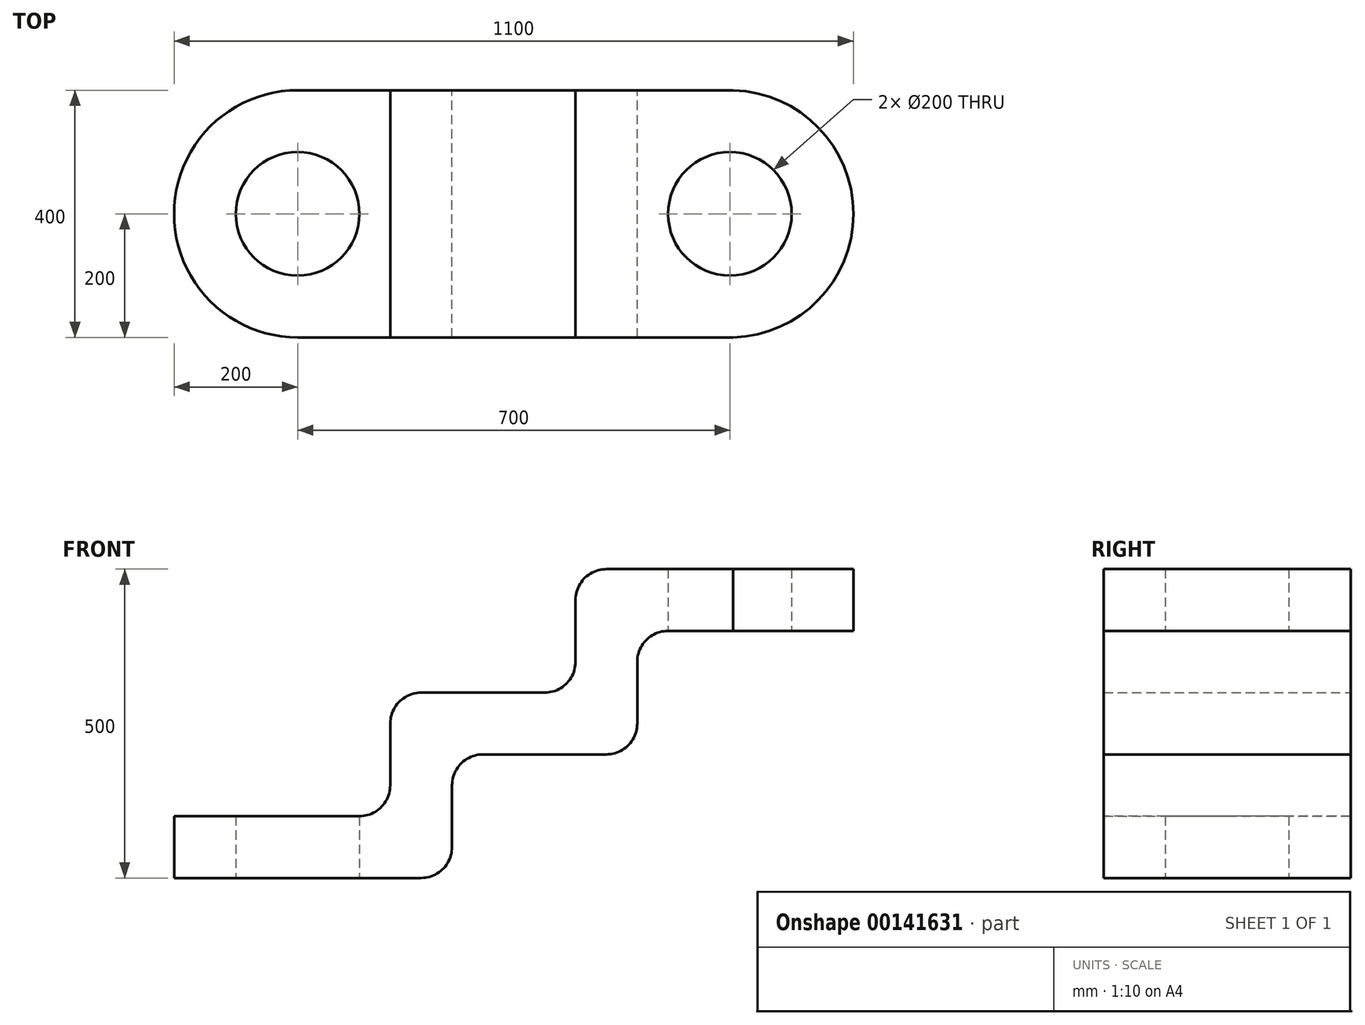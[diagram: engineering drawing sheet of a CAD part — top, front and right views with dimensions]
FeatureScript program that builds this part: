
annotation { "Feature Type Name" : "Feature", "Feature Type Description" : "" }
export const myFeature = defineFeature(function(context is Context, id is Id, definition is map)
    precondition{}
    {
        {
            var Q0;
            Q0=qCreatedBy(makeId("Top.planeOp"),FACE);
            var sketch = newSketch(context, id + "F0", { "sketchPlane" : qUnion([Q0])});
            skCircle(sketch, "E0", {"center": v(-350, 0) * mm, "radius": 100 * mm});
            skLineSegment(sketch, "E1", {"start": v(0, 0) * mm, "end": v(0, 164.51) * mm, "construction": true});
            skCircle(sketch, "E2.MirrorC", {"center": v(350, 0) * mm, "radius": 100 * mm});
            skArc(sketch, "E3", {"start": v(-349.98, 200) * mm, "mid": v(-550, 0) * mm, "end": v(-349.98, -200) * mm});
            skArc(sketch, "E4.MirrorC", {"start": v(344.9, 199.93) * mm, "mid": v(550, 0) * mm, "end": v(344.9, -199.93) * mm});
            skLineSegment(sketch, "E5", {"start": v(355.14, 199.93) * mm, "end": v(-349.98, 200) * mm});
            skLineSegment(sketch, "E6.MirrorCS", {"start": v(355.14, -199.93) * mm, "end": v(-349.98, -200) * mm});
            skSolve(sketch);
        }
        {
            var Q0;
            Q0=makeQuery(id+"F0.imprint","IMPRINT",FACE,{"disambiguationData":[TD([[makeQuery(id+"F0.imprint","IMPRINT",EDGE,{"derivedFrom":sQuery(id+"F0.wireOp",EDGE,"E0")}),-1.0]])]});
            extrude(context, id + "F1", {"entities" : qUnion([Q0]), "depth" : 500 * mm});
        }
        {
            var Q0;
            Q0=qCreatedBy(makeId("Front.planeOp"),FACE);
            var sketch = newSketch(context, id + "F2", { "sketchPlane" : qUnion([Q0])});
            skLineSegment(sketch, "E7", {"start": v(-550, 0) * mm, "end": v(-150, 0) * mm});
            skLineSegment(sketch, "E8.0", {"start": v(-550, 100) * mm, "end": v(-250, 100) * mm});
            skLineSegment(sketch, "E9.0", {"start": v(-150, 300) * mm, "end": v(50, 300) * mm});
            skLineSegment(sketch, "E10.0", {"start": v(150, 500) * mm, "end": v(550, 500) * mm});
            skLineSegment(sketch, "E11", {"start": v(-550, 0) * mm, "end": v(-550, 100) * mm});
            skLineSegment(sketch, "E12.0", {"start": v(-100, 50) * mm, "end": v(-100, 150) * mm});
            skLineSegment(sketch, "E13.0", {"start": v(-200, 150) * mm, "end": v(-200, 250) * mm});
            skLineSegment(sketch, "E14.0", {"start": v(100, 350) * mm, "end": v(100, 450) * mm});
            skLineSegment(sketch, "E15.0", {"start": v(200, 250) * mm, "end": v(200, 350) * mm});
            skLineSegment(sketch, "E16.trimOffspring", {"start": v(-50, 200) * mm, "end": v(150, 200) * mm});
            skLineSegment(sketch, "E17", {"start": v(550, 500) * mm, "end": v(550, 400) * mm});
            skLineSegment(sketch, "E18.trimOffspring", {"start": v(250, 400) * mm, "end": v(550, 400) * mm});
            skPoint(sketch, "E19.visualSharp", {"position": v(-200, 100) * mm});
            skArc(sketch, "E19.filletArc", {"start": v(-250, 100) * mm, "mid": v(-214.64, 114.64) * mm, "end": v(-200, 150) * mm});
            skPoint(sketch, "E20.visualSharp", {"position": v(-200, 300) * mm});
            skArc(sketch, "E20.filletArc", {"start": v(-150, 300) * mm, "mid": v(-185.36, 285.36) * mm, "end": v(-200, 250) * mm});
            skPoint(sketch, "E21.visualSharp", {"position": v(-100, 0) * mm});
            skArc(sketch, "E21.filletArc", {"start": v(-150, 0) * mm, "mid": v(-114.64, 14.64) * mm, "end": v(-100, 50) * mm});
            skPoint(sketch, "E22.visualSharp", {"position": v(-100, 200) * mm});
            skArc(sketch, "E22.filletArc", {"start": v(-50, 200) * mm, "mid": v(-85.36, 185.36) * mm, "end": v(-100, 150) * mm});
            skPoint(sketch, "E23.visualSharp", {"position": v(100, 300) * mm});
            skArc(sketch, "E23.filletArc", {"start": v(50, 300) * mm, "mid": v(85.36, 314.64) * mm, "end": v(100, 350) * mm});
            skPoint(sketch, "E24.visualSharp", {"position": v(200, 200) * mm});
            skArc(sketch, "E24.filletArc", {"start": v(150, 200) * mm, "mid": v(185.36, 214.64) * mm, "end": v(200, 250) * mm});
            skPoint(sketch, "E25.visualSharp", {"position": v(100, 500) * mm});
            skArc(sketch, "E25.filletArc", {"start": v(150, 500) * mm, "mid": v(114.64, 485.36) * mm, "end": v(100, 450) * mm});
            skPoint(sketch, "E26.visualSharp", {"position": v(200, 400) * mm});
            skArc(sketch, "E26.filletArc", {"start": v(250, 400) * mm, "mid": v(214.64, 385.36) * mm, "end": v(200, 350) * mm});
            skSolve(sketch);
        }
        {
            var Q0;
            Q0=makeQuery(id+"F2.imprint","IMPRINT",FACE,{"disambiguationData":[TD([[makeQuery(id+"F2.imprint","IMPRINT",EDGE,{"derivedFrom":sQuery(id+"F2.wireOp",EDGE,"E7")}),1.0]])]});
            extrude(context, id + "F3", {"entities" : qUnion([Q0]), "endBound" : BoundingType.SYMMETRIC, "depth" : 600 * mm});
        }
        {
            var Q0;
            Q0=makeQuery(id+"F1.opExtrude","SWEPT_BODY",BODY,{"disambiguationData":[OSD([sQuery(id+"F0.wireOp",EDGE,"E0"),sQuery(id+"F0.wireOp",EDGE,"E2.MirrorC"),sQuery(id+"F0.wireOp",EDGE,"E3"),sQuery(id+"F0.wireOp",EDGE,"E4.MirrorC"),sQuery(id+"F0.wireOp",EDGE,"E5"),sQuery(id+"F0.wireOp",EDGE,"E6.MirrorCS")])]});
            var Q1;
            Q1=makeQuery(id+"F3.opExtrude","SWEPT_BODY",BODY,{"disambiguationData":[OSD([sQuery(id+"F2.wireOp",EDGE,"E7"),sQuery(id+"F2.wireOp",EDGE,"E8.0"),sQuery(id+"F2.wireOp",EDGE,"E9.0"),sQuery(id+"F2.wireOp",EDGE,"E10.0"),sQuery(id+"F2.wireOp",EDGE,"E11"),sQuery(id+"F2.wireOp",EDGE,"E12.0"),sQuery(id+"F2.wireOp",EDGE,"E13.0"),sQuery(id+"F2.wireOp",EDGE,"E14.0"),sQuery(id+"F2.wireOp",EDGE,"E15.0"),sQuery(id+"F2.wireOp",EDGE,"E16.trimOffspring"),sQuery(id+"F2.wireOp",EDGE,"E17"),sQuery(id+"F2.wireOp",EDGE,"E18.trimOffspring"),sQuery(id+"F2.wireOp",EDGE,"E19.filletArc"),sQuery(id+"F2.wireOp",EDGE,"E20.filletArc"),sQuery(id+"F2.wireOp",EDGE,"E21.filletArc"),sQuery(id+"F2.wireOp",EDGE,"E22.filletArc"),sQuery(id+"F2.wireOp",EDGE,"E23.filletArc"),sQuery(id+"F2.wireOp",EDGE,"E24.filletArc"),sQuery(id+"F2.wireOp",EDGE,"E25.filletArc"),sQuery(id+"F2.wireOp",EDGE,"E26.filletArc")])]});
            booleanBodies(context, id + "F4", {"operationType" : BooleanOperationType.INTERSECTION, "tools" : qUnion([Q0, Q1])});
        }
    });
